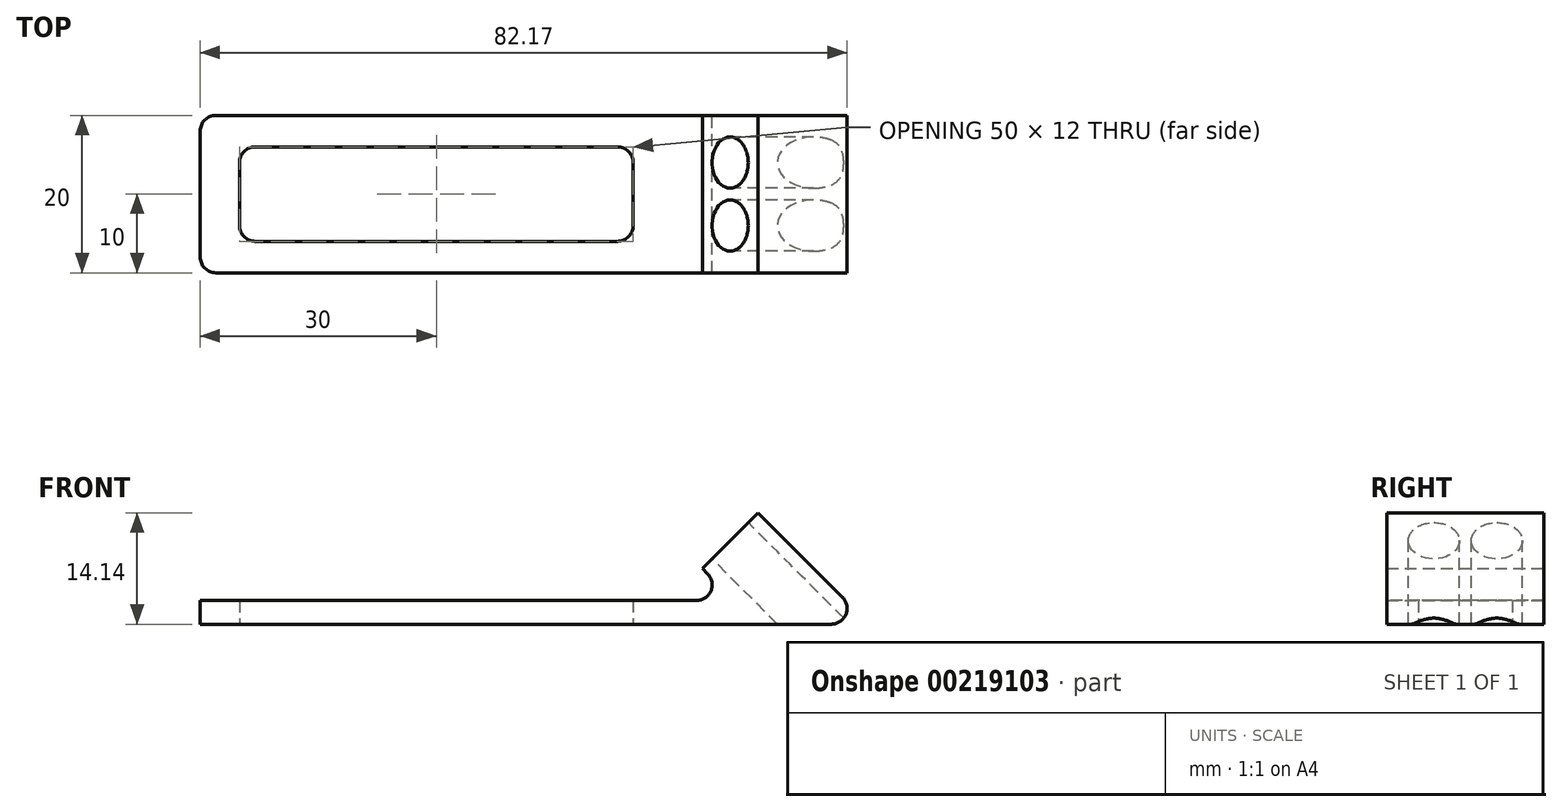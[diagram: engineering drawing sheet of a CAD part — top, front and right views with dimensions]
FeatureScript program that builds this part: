
annotation { "Feature Type Name" : "Feature", "Feature Type Description" : "" }
export const myFeature = defineFeature(function(context is Context, id is Id, definition is map)
    precondition{}
    {
        {
            var Q0;
            Q0=qCreatedBy(makeId("Front.planeOp"),FACE);
            var sketch = newSketch(context, id + "F0", { "sketchPlane" : qUnion([Q0])});
            skLineSegment(sketch, "E0", {"start": v(0, 0) * mm, "end": v(20.17, 0) * mm});
            skLineSegment(sketch, "E1", {"start": v(21.59, 3.41) * mm, "end": v(10.86, 14.14) * mm});
            skLineSegment(sketch, "E2", {"start": v(10.86, 14.14) * mm, "end": v(3.79, 7.07) * mm});
            skLineSegment(sketch, "E3", {"start": v(3.79, 7.07) * mm, "end": v(4.44, 6.41) * mm});
            skLineSegment(sketch, "E4", {"start": v(3.03, 3) * mm, "end": v(0, 3) * mm});
            skLineSegment(sketch, "E5", {"start": v(0, 3) * mm, "end": v(0, 0) * mm});
            skPoint(sketch, "E6.visualSharp", {"position": v(25, 0) * mm});
            skArc(sketch, "E6.filletArc", {"start": v(20.17, 0) * mm, "mid": v(22.02, 1.23) * mm, "end": v(21.59, 3.41) * mm});
            skPoint(sketch, "E7.visualSharp", {"position": v(7.86, 3) * mm});
            skArc(sketch, "E7.filletArc", {"start": v(3.03, 3) * mm, "mid": v(4.88, 4.23) * mm, "end": v(4.44, 6.41) * mm});
            skSolve(sketch);
        }
        {
            var Q0;
            Q0 = qSketchRegion(id + "F0", true);
            extrude(context, id + "F1", {"entities" : qUnion([Q0]), "endBound" : BoundingType.SYMMETRIC, "depth" : 20 * mm});
        }
        {
            var Q0;
            Q0=makeQuery(id+"F1.opExtrude","SWEPT_FACE",FACE,{"disambiguationData":[OSD([sQuery(id+"F0.wireOp",EDGE,"E2")])]});
            var sketch = newSketch(context, id + "F2", { "sketchPlane" : qUnion([Q0])});
            skLineSegment(sketch, "E8", {"start": v(0, 7.68) * mm, "end": v(0, 17.68) * mm, "construction": true});
            skLineSegment(sketch, "E9", {"start": v(0, 12.68) * mm, "end": v(-4, 12.68) * mm, "construction": true});
            skCircle(sketch, "E10", {"center": v(-4, 12.68) * mm, "radius": 3.25 * mm});
            skCircle(sketch, "E11.MirrorC", {"center": v(4, 12.68) * mm, "radius": 3.25 * mm});
            skSolve(sketch);
        }
        {
            var Q0;
            Q0 = qSketchRegion(id + "F2", true);
            extrude(context, id + "F3", {"entities" : qUnion([Q0]), "operationType" : NewBodyOperationType.REMOVE, "oppositeDirection" : true, "depth" : 25 * mm});
        }
        {
            var Q0;
            Q0=qCreatedBy(makeId("Top.planeOp"),FACE);
            var sketch = newSketch(context, id + "F4", { "sketchPlane" : qUnion([Q0])});
            skLineSegment(sketch, "E12.bottom", {"start": v(0, 10) * mm, "end": v(-58, 10) * mm});
            skLineSegment(sketch, "E12.top", {"start": v(0, -10) * mm, "end": v(-58, -10) * mm});
            skLineSegment(sketch, "E12.left", {"start": v(0, 10) * mm, "end": v(0, -10) * mm});
            skLineSegment(sketch, "E12.right", {"start": v(-60, 8) * mm, "end": v(-60, -8) * mm});
            skPoint(sketch, "E12.middle", {"position": v(-30, 0) * mm});
            skPoint(sketch, "E13.visualSharp", {"position": v(-60, -10) * mm});
            skArc(sketch, "E13.filletArc", {"start": v(-60, -8) * mm, "mid": v(-59.41, -9.41) * mm, "end": v(-58, -10) * mm});
            skPoint(sketch, "E14.visualSharp", {"position": v(-60, 10) * mm});
            skArc(sketch, "E14.filletArc", {"start": v(-58, 10) * mm, "mid": v(-59.41, 9.41) * mm, "end": v(-60, 8) * mm});
            skLineSegment(sketch, "E15.bottom", {"start": v(-7, 6) * mm, "end": v(-53, 6) * mm});
            skLineSegment(sketch, "E15.top", {"start": v(-7, -6) * mm, "end": v(-53, -6) * mm});
            skLineSegment(sketch, "E15.left", {"start": v(-5, 4) * mm, "end": v(-5, -4) * mm});
            skLineSegment(sketch, "E15.right", {"start": v(-55, 4) * mm, "end": v(-55, -4) * mm});
            skPoint(sketch, "E16.visualSharp", {"position": v(-55, 6) * mm});
            skArc(sketch, "E16.filletArc", {"start": v(-53, 6) * mm, "mid": v(-54.41, 5.41) * mm, "end": v(-55, 4) * mm});
            skPoint(sketch, "E17.visualSharp", {"position": v(-55, -6) * mm});
            skArc(sketch, "E17.filletArc", {"start": v(-55, -4) * mm, "mid": v(-54.41, -5.41) * mm, "end": v(-53, -6) * mm});
            skPoint(sketch, "E18.visualSharp", {"position": v(-5, -6) * mm});
            skArc(sketch, "E18.filletArc", {"start": v(-7, -6) * mm, "mid": v(-5.59, -5.41) * mm, "end": v(-5, -4) * mm});
            skPoint(sketch, "E19.visualSharp", {"position": v(-5, 6) * mm});
            skArc(sketch, "E19.filletArc", {"start": v(-5, 4) * mm, "mid": v(-5.59, 5.41) * mm, "end": v(-7, 6) * mm});
            skSolve(sketch);
        }
        {
            var Q0;
            Q0=makeQuery(id+"F4.imprint","IMPRINT",FACE,{"disambiguationData":[TD([[makeQuery(id+"F4.imprint","IMPRINT",EDGE,{"derivedFrom":sQuery(id+"F4.wireOp",EDGE,"E12.bottom")}),1.0]])]});
            extrude(context, id + "F5", {"entities" : qUnion([Q0]), "operationType" : NewBodyOperationType.ADD, "depth" : 3 * mm});
        }
    });
